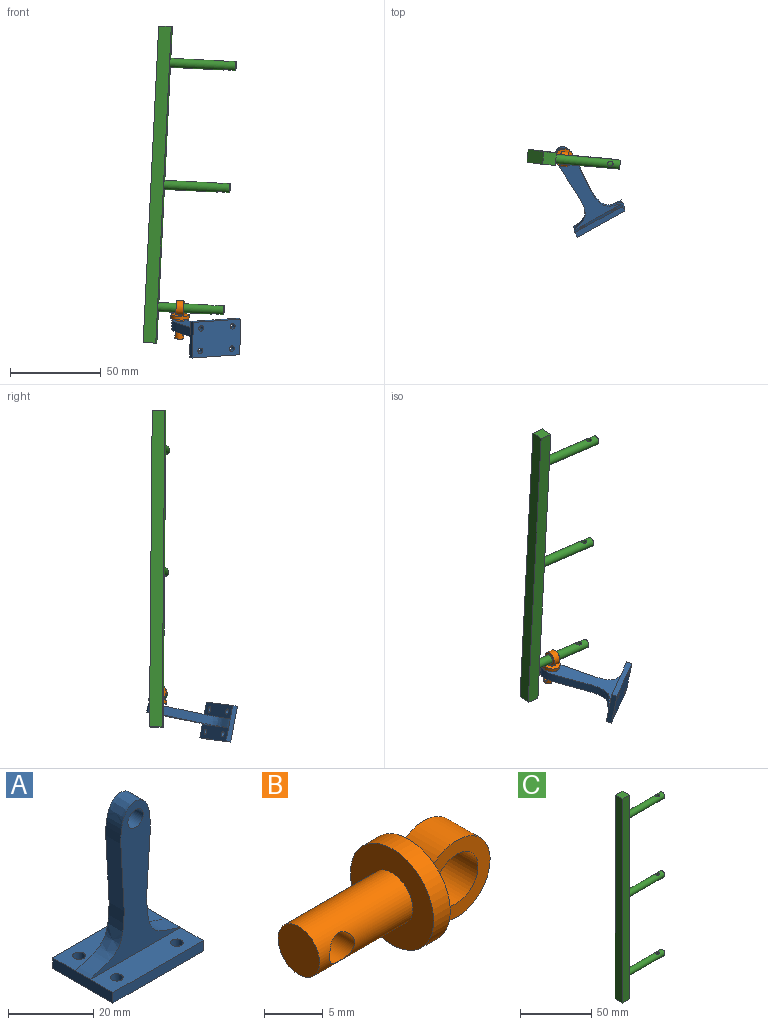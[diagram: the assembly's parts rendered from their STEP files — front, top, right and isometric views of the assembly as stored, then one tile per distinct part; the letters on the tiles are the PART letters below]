
ASSEMBLY  parts=3 mates=2
PART A: 15 faces, bbox 30x20x48.1 mm
  f0: plane 30x7.5mm, normal (0,0,1), area 210.9mm2, adj f2,f4,f6,f10,f11,f14
  f1: plane 30x7.5mm, normal (0,0,1), area 210.9mm2, adj f2,f4,f5,f9,f12,f13
  f2: plane 20x3mm, normal (-1,0,0), area 60mm2, adj f0,f1,f3,f5,f6,f7
  f3: plane 30x20mm, normal (0,0,-1), area 571.7mm2, adj f2,f4,f5,f6,f11,f12,f13,f14
  f4: plane 20x3mm, normal (1,0,0), area 60mm2, adj f0,f1,f3,f5,f6,f7
  f5: plane 30x3mm, normal (0,-1,0), area 90mm2, adj f1,f2,f3,f4
  f6: plane 30x3mm, normal (0,1,0), area 90mm2, adj f0,f2,f3,f4
  f7: extruded ~43.88x30mm, area 526.7mm2, adj f2,f4,f9,f10
  f8: cylinder r=2.55mm len=5.1mm, axis (0,1,0), area 80.1mm2, adj f9,f10
  f9: plane 45.13x30mm, normal (0,-1,0), area 397.3mm2, adj f1,f7,f8
  f10: plane 45.13x30mm, normal (0,1,0), area 397.3mm2, adj f0,f7,f8
  f11: cylinder r=1.5mm len=3mm, axis (0,0,1), area 28.3mm2, adj f0,f3
  f12: cylinder r=1.5mm len=3mm, axis (0,0,1), area 28.3mm2, adj f1,f3
  f13: cylinder r=1.5mm len=3mm, axis (0,0,1), area 28.3mm2, adj f1,f3
  f14: cylinder r=1.5mm len=3mm, axis (0,0,1), area 28.3mm2, adj f0,f3
PART B: 11 faces, bbox 21x10x10 mm
  f0: cylinder r=2.5mm len=5mm, axis (-1,0,0), area 13.1mm2, adj f1,f7,f8,f9,f10
  f1: plane 10x10mm, normal (1,0,0), area 58.9mm2, adj f0,f2
  f2: cylinder r=5mm len=10mm, axis (-1,0,0), area 62.8mm2, adj f1,f3
  f3: plane 10x10mm, normal (-1,0,0), area 58.9mm2, adj f2,f4
  f4: cylinder r=2.5mm len=11.21mm, axis (-1,0,0), area 161.2mm2, adj f3,f5,f6
  f5: plane 5x5mm, normal (-1,0,0), area 19.6mm2, adj f4
  f6: cylinder r=1.5mm len=5mm, axis (0,-1,0), area 42.5mm2, adj f4
  f7: cylinder r=4mm len=8mm, axis (0,1,0), area 81.8mm2, adj f0,f8,f9
  f8: plane 8x7.71mm, normal (0,-1,0), area 25.3mm2, adj f0,f7,f10
  f9: plane 8x7.71mm, normal (0,1,0), area 25.3mm2, adj f0,f7,f10
  f10: cylinder r=2.55mm len=5.1mm, axis (0,1,0), area 66.2mm2, adj f0,f8,f9
PART C: 15 faces, bbox 43.5x7x175 mm
  f0: cylinder r=2.5mm len=36.5mm, axis (-1,0,0), area 558.4mm2, adj f1,f2,f4
  f1: plane 5x5mm, normal (1,0,0), area 19.6mm2, adj f0
  f2: cylinder r=1.5mm len=5mm, axis (0,0,1), area 42.5mm2, adj f0
  f3: plane 175x7mm, normal (0,-1,0), area 1225mm2, adj f4,f6,f10,f11
  f4: plane 175x7mm, normal (1,0,0), area 1166.7mm2, adj f0,f3,f5,f9,f10,f11,f14
  f5: plane 175x7mm, normal (0,1,0), area 1225mm2, adj f4,f6,f10,f11
  f6: plane 175x7mm, normal (-1,0,0), area 1225mm2, adj f3,f5,f10,f11
  f7: plane 5x5mm, normal (1,0,0), area 19.6mm2, adj f9
  f8: cylinder r=1.5mm len=5mm, axis (0,0,1), area 42.5mm2, adj f9
  f9: cylinder r=2.5mm len=36.5mm, axis (-1,0,0), area 558.4mm2, adj f4,f7,f8
  f10: plane 7x7mm, normal (0,0,1), area 49mm2, adj f3,f4,f5,f6
  f11: plane 7x7mm, normal (0,0,-1), area 49mm2, adj f3,f4,f5,f6
  f12: plane 4.93x4.93mm, normal (1,0,0), area 19.1mm2, adj f14
  f13: cylinder r=1.5mm len=4.93mm, axis (0,0,1), area 41.8mm2, adj f14
  f14: cylinder r=2.46mm len=36.5mm, axis (-1,0,0), area 550.1mm2, adj f4,f12,f13
PLACE A rot(axis=(-0.93,-0.27,0.26),83.4deg) t=(-65.76,-5.17,33.33)mm
PLACE B rot(axis=(-0.57,-0.49,-0.65),116deg) t=(-73.76,8.21,42.1)mm
PLACE C rot(axis=(0.06,0.49,-0.87),5.8deg) t=(-89.14,8.89,51.6)mm
MATE cylindrical B.f7 <-> C.f14  axis (0.99,-0.09,-0.05) through (-71.65,7.35,45.72)mm
MATE cylindrical A.f8 <-> B.f0  axis (-0.03,0.18,-0.98) through (-74.04,9.74,33.82)mm
